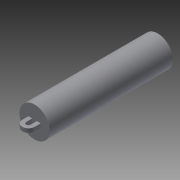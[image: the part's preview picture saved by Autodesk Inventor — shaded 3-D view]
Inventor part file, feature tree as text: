
AUTODESK INVENTOR PART (.ipt)
format: ipt  version: 2014 (Build 180170000, 170)  size: 100,352 bytes
history: native  units: in
note: dims shown in document units (in); Inventor stores cm internally (conversion verified against a paired STEP export)
features: extrude x3, sketch x3
ambient origin geometry x8: Origin, YZ Plane, XZ Plane, XY Plane, X Axis, Y Axis, Z Axis, Center Point
bodies: Solid1 (feature_tree)
feature tree (6):
  extrude  "Extrusion1"  Depth=10.0in TaperAngle=0.0deg
  extrude  "Extrusion2"  Depth=0.312in
  extrude  "Extrusion3"  Depth=0.5in
  sketch  "Sketch1"  dims[d0=2.462in d1=10.0in d2=0.0in]
  sketch  "Sketch2"  dims[d3=0.312in d4=0.156in]
  sketch  "Sketch3"  dims[d5=0.5in d6=0.5in d7=1.0in d8=0.0in d9=0.312in d10=1.0in d11=0.0in]
